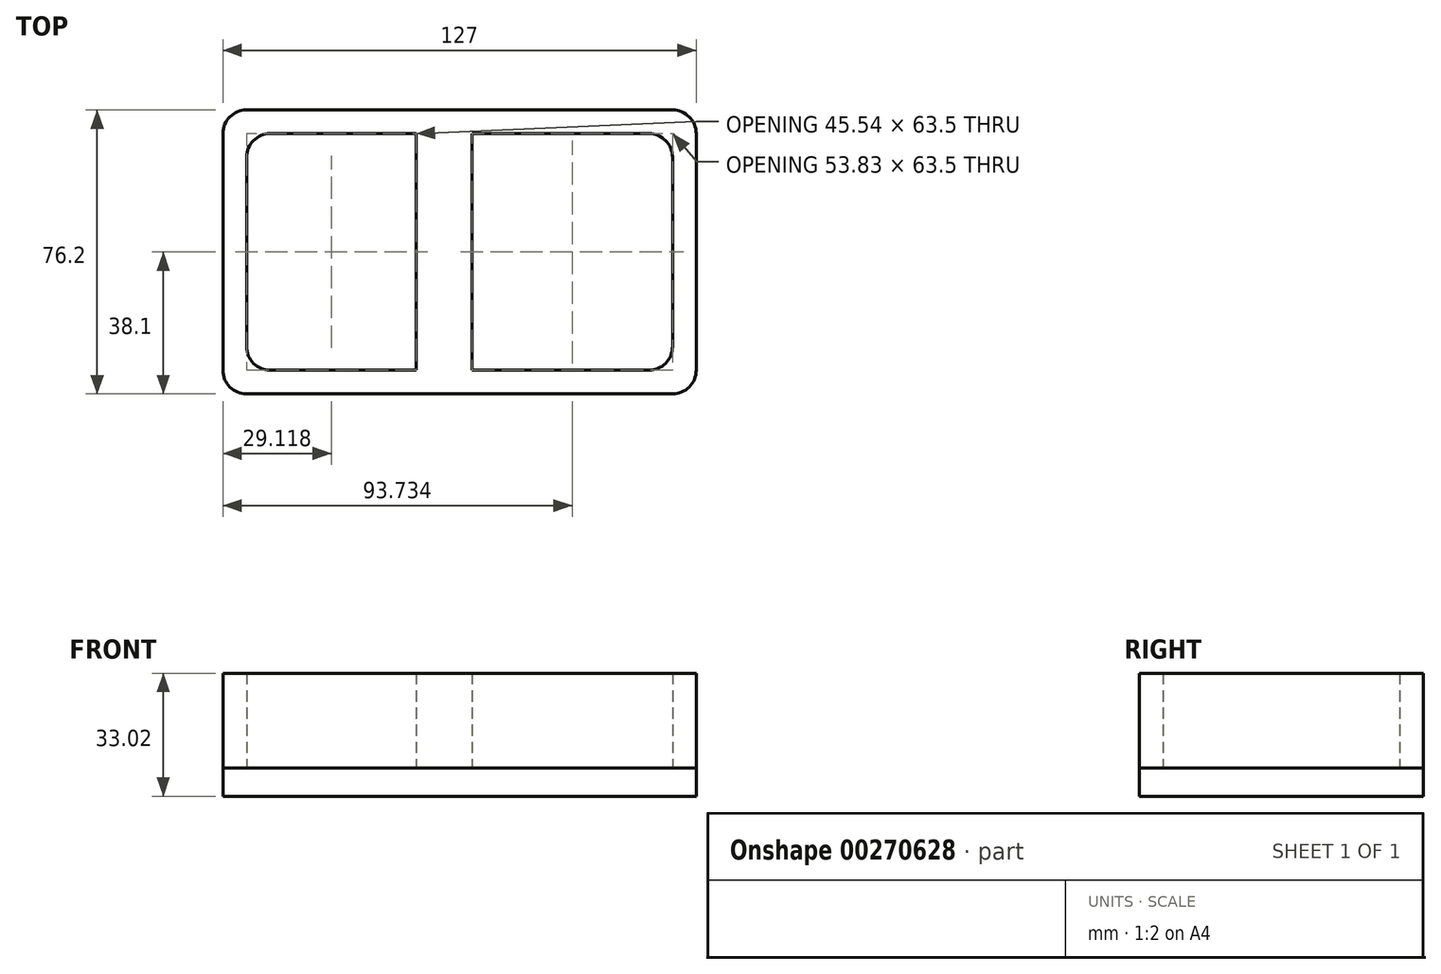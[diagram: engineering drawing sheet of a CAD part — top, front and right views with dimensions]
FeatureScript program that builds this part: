
annotation { "Feature Type Name" : "Feature", "Feature Type Description" : "" }
export const myFeature = defineFeature(function(context is Context, id is Id, definition is map)
    precondition{}
    {
        {
            var Q0;
            Q0=qCreatedBy(makeId("Top.planeOp"),FACE);
            var sketch = newSketch(context, id + "F0", { "sketchPlane" : qUnion([Q0])});
            skLineSegment(sketch, "E0.bottom", {"start": v(57.15, 38.1) * mm, "end": v(-57.15, 38.1) * mm});
            skLineSegment(sketch, "E0.top", {"start": v(57.15, -38.1) * mm, "end": v(-57.15, -38.1) * mm});
            skLineSegment(sketch, "E0.left", {"start": v(63.5, 31.75) * mm, "end": v(63.5, -31.75) * mm});
            skLineSegment(sketch, "E0.right", {"start": v(-63.5, 31.75) * mm, "end": v(-63.5, -31.75) * mm});
            skPoint(sketch, "E0.middle", {"position": v(0, 0) * mm});
            skLineSegment(sketch, "E1.bottom", {"start": v(50.8, 31.75) * mm, "end": v(-50.8, 31.75) * mm});
            skLineSegment(sketch, "E1.top", {"start": v(50.8, -31.75) * mm, "end": v(-50.8, -31.75) * mm});
            skLineSegment(sketch, "E1.left", {"start": v(57.15, 25.4) * mm, "end": v(57.15, -25.4) * mm});
            skLineSegment(sketch, "E1.right", {"start": v(-57.15, 25.4) * mm, "end": v(-57.15, -25.4) * mm});
            skPoint(sketch, "E2.visualSharp", {"position": v(-57.15, 31.75) * mm});
            skArc(sketch, "E2.filletArc", {"start": v(-50.8, 31.75) * mm, "mid": v(-55.3, 29.9) * mm, "end": v(-57.15, 25.4) * mm});
            skPoint(sketch, "E3.visualSharp", {"position": v(-63.5, 38.1) * mm});
            skArc(sketch, "E3.filletArc", {"start": v(-57.15, 38.1) * mm, "mid": v(-61.64, 36.24) * mm, "end": v(-63.5, 31.75) * mm});
            skPoint(sketch, "E4.visualSharp", {"position": v(-57.15, -31.75) * mm});
            skArc(sketch, "E4.filletArc", {"start": v(-57.15, -25.4) * mm, "mid": v(-55.3, -29.9) * mm, "end": v(-50.8, -31.75) * mm});
            skPoint(sketch, "E5.visualSharp", {"position": v(57.15, -31.75) * mm});
            skArc(sketch, "E5.filletArc", {"start": v(50.8, -31.75) * mm, "mid": v(55.3, -29.9) * mm, "end": v(57.15, -25.4) * mm});
            skPoint(sketch, "E6.visualSharp", {"position": v(57.15, 31.75) * mm});
            skArc(sketch, "E6.filletArc", {"start": v(57.15, 25.4) * mm, "mid": v(55.3, 29.9) * mm, "end": v(50.8, 31.75) * mm});
            skPoint(sketch, "E7.visualSharp", {"position": v(63.5, 38.1) * mm});
            skArc(sketch, "E7.filletArc", {"start": v(63.5, 31.75) * mm, "mid": v(61.64, 36.24) * mm, "end": v(57.15, 38.1) * mm});
            skPoint(sketch, "E8.visualSharp", {"position": v(63.5, -38.1) * mm});
            skArc(sketch, "E8.filletArc", {"start": v(57.15, -38.1) * mm, "mid": v(61.64, -36.24) * mm, "end": v(63.5, -31.75) * mm});
            skPoint(sketch, "E9.visualSharp", {"position": v(-63.5, -38.1) * mm});
            skArc(sketch, "E9.filletArc", {"start": v(-63.5, -31.75) * mm, "mid": v(-61.64, -36.24) * mm, "end": v(-57.15, -38.1) * mm});
            skLineSegment(sketch, "E10", {"start": v(-11.61, 31.75) * mm, "end": v(-11.61, -31.75) * mm});
            skLineSegment(sketch, "E11", {"start": v(3.32, 31.75) * mm, "end": v(3.32, -31.75) * mm});
            skSolve(sketch);
        }
        {
            var Q0;
            {var subQ0=sQuery(id+"F0.wireOp",EDGE,"E10");Q0=makeQuery(id+"F0.imprint","IMPRINT",FACE,{"disambiguationData":[TD([[makeQuery(id+"F0.imprint","IMPRINT",EDGE,{"derivedFrom":subQ0}),1.0]])]});}
            var Q1;
            Q1=makeQuery(id+"F0.imprint","IMPRINT",FACE,{"disambiguationData":[TD([[makeQuery(id+"F0.imprint","IMPRINT",EDGE,{"derivedFrom":sQuery(id+"F0.wireOp",EDGE,"E0.bottom")}),1.0]])]});
            extrude(context, id + "F1", {"entities" : qUnion([Q0, Q1]), "depth" : 25.4 * mm});
        }
        {
            var Q0;
            Q0=makeQuery(id+"F0.imprint","IMPRINT",FACE,{"disambiguationData":[TD([[makeQuery(id+"F0.imprint","IMPRINT",EDGE,{"derivedFrom":sQuery(id+"F0.wireOp",EDGE,"E0.bottom")}),1.0]])]});
            var Q1;
            Q1=makeQuery(id+"F0.imprint","IMPRINT",FACE,{"disambiguationData":[TD([[makeQuery(id+"F0.imprint","IMPRINT",EDGE,{"derivedFrom":sQuery(id+"F0.wireOp",EDGE,"E1.left")}),-1.0]])]});
            var Q2;
            {var subQ0=sQuery(id+"F0.wireOp",EDGE,"E10");Q2=makeQuery(id+"F0.imprint","IMPRINT",FACE,{"disambiguationData":[TD([[makeQuery(id+"F0.imprint","IMPRINT",EDGE,{"derivedFrom":subQ0}),1.0]])]});}
            var Q3;
            Q3=makeQuery(id+"F0.imprint","IMPRINT",FACE,{"disambiguationData":[TD([[makeQuery(id+"F0.imprint","IMPRINT",EDGE,{"derivedFrom":sQuery(id+"F0.wireOp",EDGE,"E1.right")}),1.0]])]});
            extrude(context, id + "F2", {"entities" : qUnion([Q0, Q1, Q2, Q3]), "oppositeDirection" : true, "depth" : 7.62 * mm});
        }
    });
